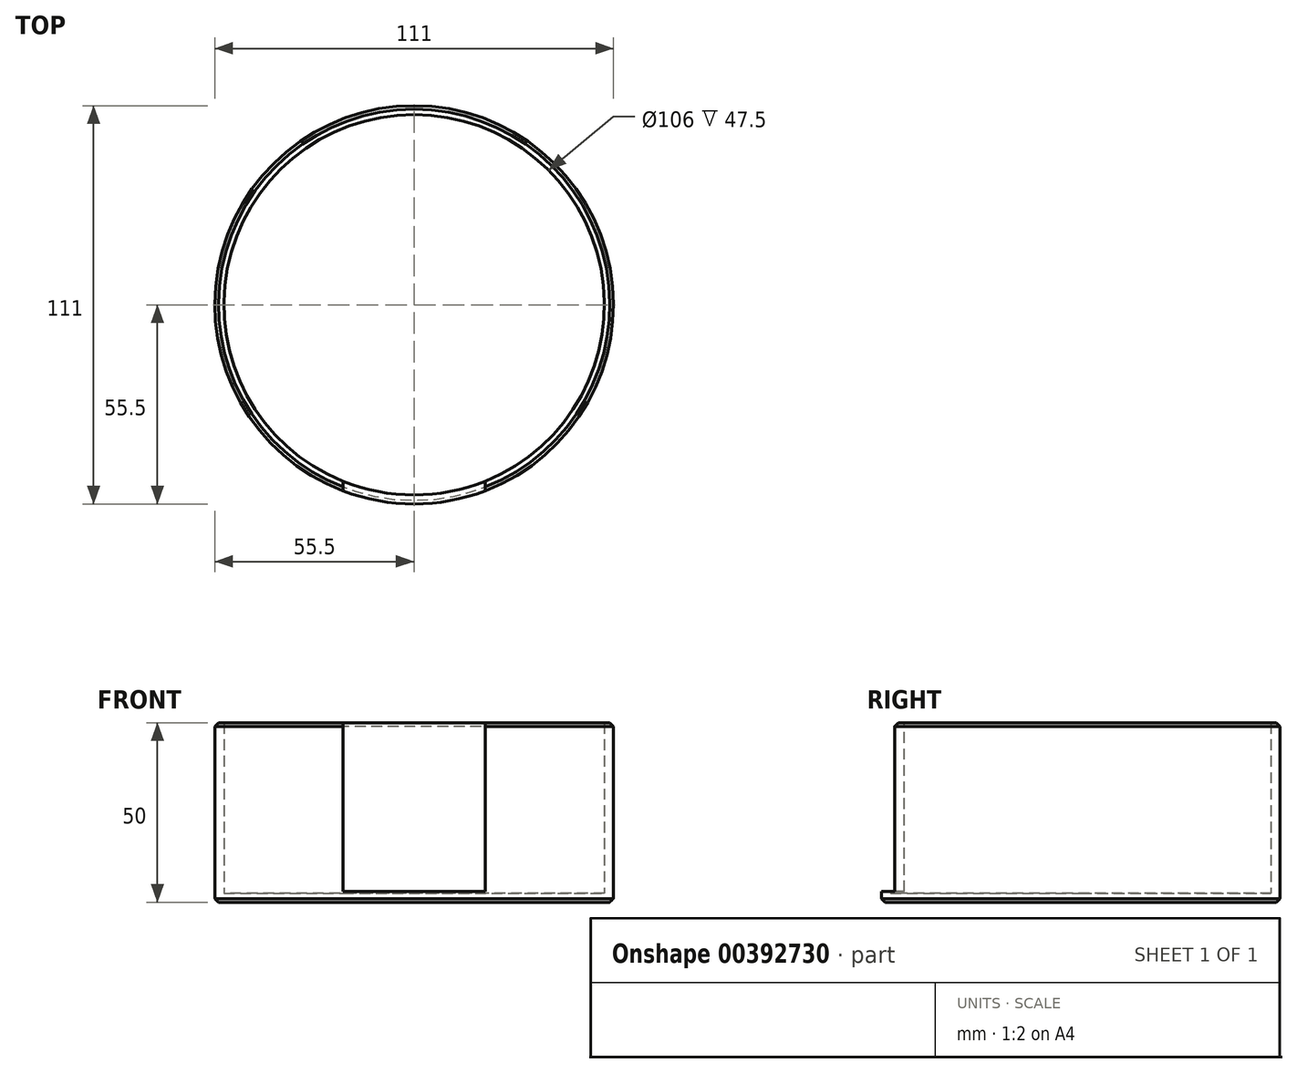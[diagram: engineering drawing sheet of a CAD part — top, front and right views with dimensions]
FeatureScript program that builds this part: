
annotation { "Feature Type Name" : "Feature", "Feature Type Description" : "" }
export const myFeature = defineFeature(function(context is Context, id is Id, definition is map)
    precondition{}
    {
        {
            var Q0;
            Q0=qCreatedBy(makeId("Top.planeOp"),FACE);
            var sketch = newSketch(context, id + "F0", { "sketchPlane" : qUnion([Q0])});
            skCircle(sketch, "E0", {"center": v(0, 0) * mm, "radius": 55.5 * mm});
            skSolve(sketch);
        }
        {
            var Q0;
            Q0=makeQuery(id+"F0.imprint","IMPRINT",FACE,{"disambiguationData":[TD([[makeQuery(id+"F0.imprint","IMPRINT",EDGE,{"derivedFrom":sQuery(id+"F0.wireOp",EDGE,"E0")}),1.0]])]});
            extrude(context, id + "F1", {"entities" : qUnion([Q0]), "depth" : 50 * mm});
        }
        {
            var Q0;
            Q0=makeQuery(id+"F1.opExtrude","CAP_FACE",FACE,{"disambiguationData":[OSD([sQuery(id+"F0.wireOp",EDGE,"E0")])],"isStart":false});
            shell(context, id + "F2", {"entities" : qUnion([Q0]), "thickness" : 2.5 * mm});
        }
        {
            var Q0;
            Q0=makeQuery(id+"F1.opExtrude","CAP_FACE",FACE,{"disambiguationData":[OSD([sQuery(id+"F0.wireOp",EDGE,"E0")])],"isStart":false});
            var sketch = newSketch(context, id + "F3", { "sketchPlane" : qUnion([Q0])});
            skLineSegment(sketch, "E1", {"start": v(0, -45.3) * mm, "end": v(-19.82, -45.3) * mm});
            skLineSegment(sketch, "E2", {"start": v(-19.82, -45.3) * mm, "end": v(-19.82, -57.28) * mm});
            skLineSegment(sketch, "E3", {"start": v(-19.82, -57.28) * mm, "end": v(0, -57.28) * mm});
            skLineSegment(sketch, "E4.MirrorCS", {"start": v(19.82, -57.28) * mm, "end": v(0, -57.28) * mm});
            skLineSegment(sketch, "E5.MirrorCS", {"start": v(0, -45.3) * mm, "end": v(19.82, -45.3) * mm});
            skLineSegment(sketch, "E6.MirrorCS", {"start": v(19.82, -45.3) * mm, "end": v(19.82, -57.28) * mm});
            skSolve(sketch);
        }
        {
            var Q0;
            {var subQ4=sQuery(id+"F3.wireOp",EDGE,"E3");Q0=makeQuery(id+"F3.imprint","IMPRINT",FACE,{"disambiguationData":[TD([[makeQuery(id+"F3.imprint","IMPRINT",EDGE,{"derivedFrom":subQ4}),1.0]])]});}
            var Q1;
            {var subQ0=sQuery(id+"F3.wireOp",EDGE,"E2");var subQ1=sQuery(id+"F0.wireOp",EDGE,"E0");var subQ2=makeQuery(id+"F1.opExtrude","CAP_EDGE",EDGE,{"disambiguationData":[OSD([subQ1])],"isStart":false});var subQ3=makeQuery(id+"F3.imprint","INTERSECT",VERTEX,{"derivedFrom":[subQ2,subQ0]});Q1=makeQuery(id+"F3.imprint","IMPRINT",FACE,{"disambiguationData":[TD([[makeQuery(id+"F3.imprint","IMPRINT",EDGE,{"disambiguationData":[TD([[subQ3,-1.0]])],"derivedFrom":subQ2}),1.0]])]});}
            extrude(context, id + "F4", {"entities" : qUnion([Q0, Q1]), "operationType" : NewBodyOperationType.REMOVE, "oppositeDirection" : true, "depth" : 47 * mm});
        }
        {
            var Q0;
            Q0=makeQuery(id+"F1.opExtrude","CAP_EDGE",EDGE,{"disambiguationData":[OSD([sQuery(id+"F0.wireOp",EDGE,"E0")])],"isStart":true});
            var Q1;
            Q1=makeQuery(id+"F1.opExtrude","CAP_EDGE",EDGE,{"disambiguationData":[OSD([sQuery(id+"F0.wireOp",EDGE,"E0")])],"isStart":false});
            chamfer(context, id + "F5", {"entities" : qUnion([Q0, Q1]), "width" : 1 * mm, "tangentPropagation" : true});
        }
    });
